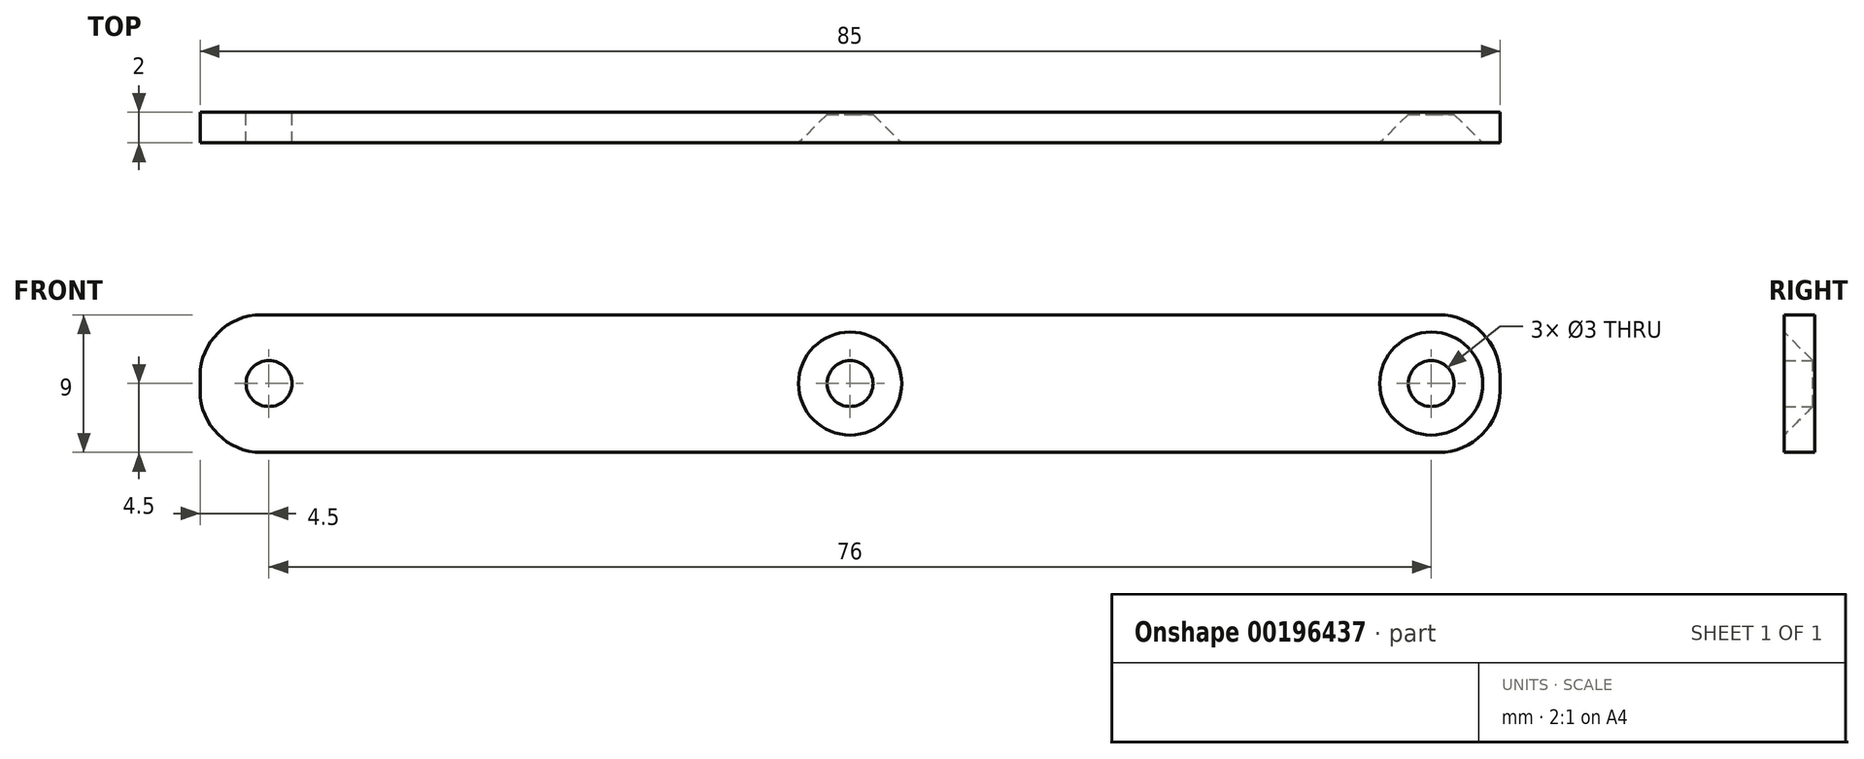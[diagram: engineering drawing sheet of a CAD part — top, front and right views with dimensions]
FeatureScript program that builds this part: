
annotation { "Feature Type Name" : "Feature", "Feature Type Description" : "" }
export const myFeature = defineFeature(function(context is Context, id is Id, definition is map)
    precondition{}
    {
        {
            var Q0;
            Q0=qCreatedBy(makeId("Front.planeOp"),FACE);
            var sketch = newSketch(context, id + "F0", { "sketchPlane" : qUnion([Q0])});
            skLineSegment(sketch, "E0.bottom", {"start": v(42.5, 4.5) * mm, "end": v(-42.5, 4.5) * mm});
            skLineSegment(sketch, "E0.top", {"start": v(42.5, -4.5) * mm, "end": v(-42.5, -4.5) * mm});
            skLineSegment(sketch, "E0.left", {"start": v(42.5, 4.5) * mm, "end": v(42.5, -4.5) * mm});
            skLineSegment(sketch, "E0.right", {"start": v(-42.5, 4.5) * mm, "end": v(-42.5, -4.5) * mm});
            skPoint(sketch, "E0.middle", {"position": v(0, 0) * mm});
            skCircle(sketch, "E1", {"center": v(0, 0) * mm, "radius": 1.5 * mm});
            skCircle(sketch, "E2", {"center": v(38, 0) * mm, "radius": 1.5 * mm});
            skCircle(sketch, "E3", {"center": v(-38, 0) * mm, "radius": 1.5 * mm});
            skSolve(sketch);
        }
        {
            var Q0;
            Q0=qSketchRegion(id+"F0",true);
            extrude(context, id + "F1", {"entities" : qUnion([Q0]), "depth" : 2 * mm});
        }
        {
            var Q0;
            Q0=makeQuery(id+"F1.opExtrude","SWEPT_EDGE",EDGE,{"disambiguationData":[OSD([sQuery(id+"F0.wireOp",EDGE,"E0.bottom"),sQuery(id+"F0.wireOp",EDGE,"E0.right")])]});
            var Q1;
            Q1=makeQuery(id+"F1.opExtrude","SWEPT_EDGE",EDGE,{"disambiguationData":[OSD([sQuery(id+"F0.wireOp",EDGE,"E0.top"),sQuery(id+"F0.wireOp",EDGE,"E0.right")])]});
            var Q2;
            Q2=makeQuery(id+"F1.opExtrude","SWEPT_EDGE",EDGE,{"disambiguationData":[OSD([sQuery(id+"F0.wireOp",EDGE,"E0.top"),sQuery(id+"F0.wireOp",EDGE,"E0.left")])]});
            var Q3;
            Q3=makeQuery(id+"F1.opExtrude","SWEPT_EDGE",EDGE,{"disambiguationData":[OSD([sQuery(id+"F0.wireOp",EDGE,"E0.bottom"),sQuery(id+"F0.wireOp",EDGE,"E0.left")])]});
            fillet(context, id + "F2", {"entities" : qUnion([Q0, Q1, Q2, Q3]), "radius" : 4 * mm, "tangentPropagation" : true, "allowEdgeOverflow" : false});
        }
        {
            var Q0;
            Q0=makeQuery(id+"F1.opExtrude","CAP_EDGE",EDGE,{"disambiguationData":[OSD([sQuery(id+"F0.wireOp",EDGE,"E2")])],"isStart":false});
            var Q1;
            Q1=makeQuery(id+"F1.opExtrude","CAP_EDGE",EDGE,{"disambiguationData":[OSD([sQuery(id+"F0.wireOp",EDGE,"E1")])],"isStart":false});
            chamfer(context, id + "F3", {"entities" : qUnion([Q0, Q1]), "width" : 1.87 * mm, "tangentPropagation" : true});
        }
    });
